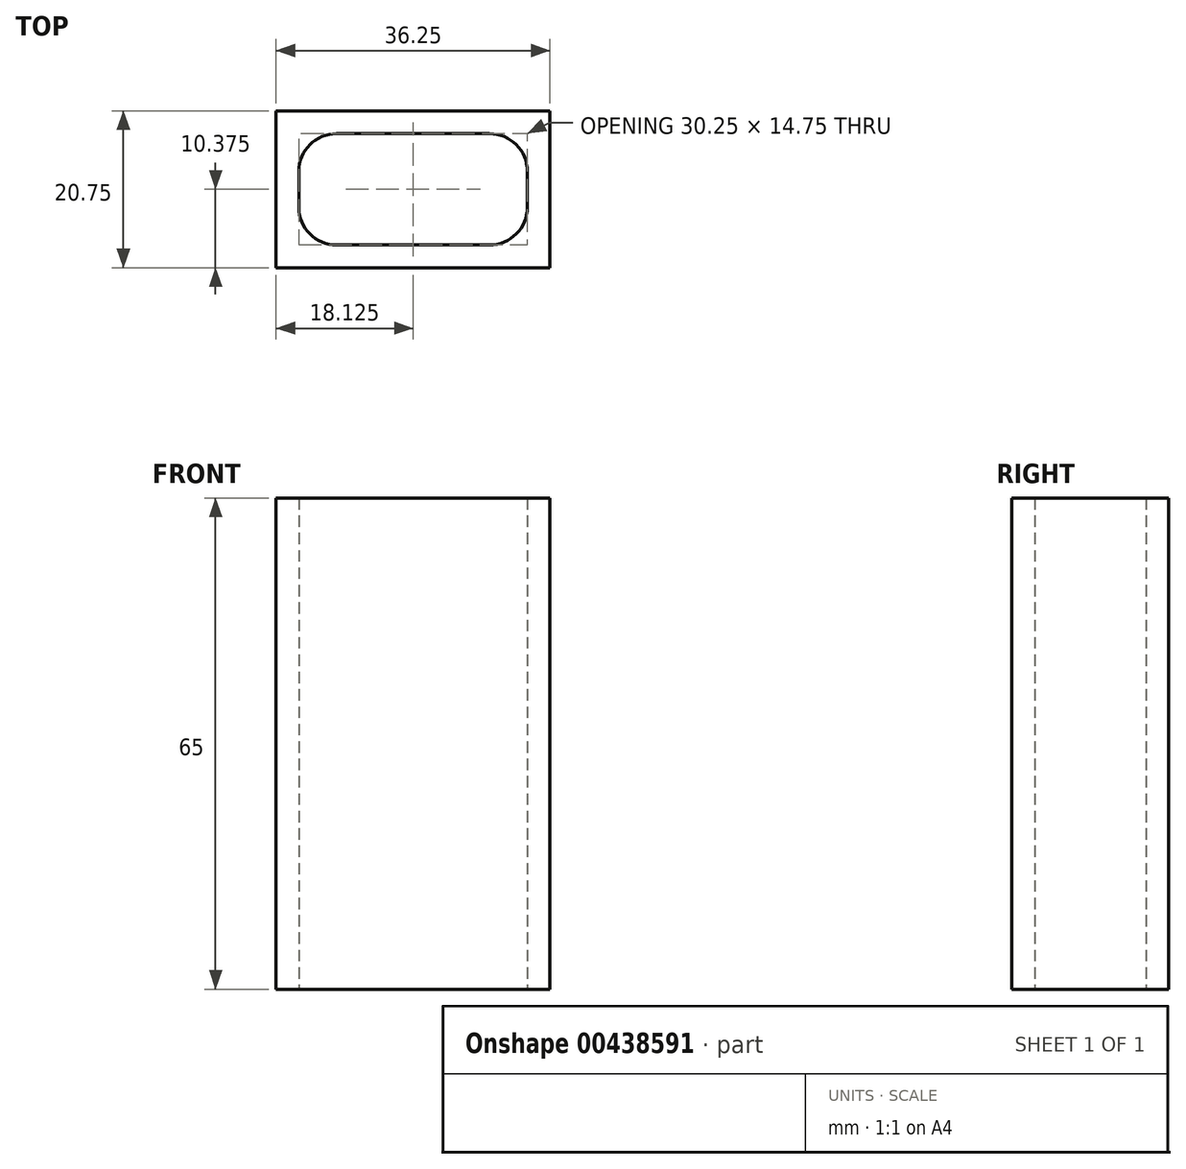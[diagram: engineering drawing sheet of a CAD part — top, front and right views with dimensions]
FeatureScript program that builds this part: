
annotation { "Feature Type Name" : "Feature", "Feature Type Description" : "" }
export const myFeature = defineFeature(function(context is Context, id is Id, definition is map)
    precondition{}
    {
        {
            var Q0;
            Q0=qCreatedBy(makeId("Top.planeOp"),FACE);
            var sketch = newSketch(context, id + "F0", { "sketchPlane" : qUnion([Q0])});
            skLineSegment(sketch, "E0.bottom", {"start": v(5, 0) * mm, "end": v(25.25, 0) * mm});
            skLineSegment(sketch, "E0.top", {"start": v(5, 14.75) * mm, "end": v(25.25, 14.75) * mm});
            skLineSegment(sketch, "E0.left", {"start": v(0, 5) * mm, "end": v(0, 9.75) * mm});
            skLineSegment(sketch, "E0.right", {"start": v(30.25, 5) * mm, "end": v(30.25, 9.75) * mm});
            skPoint(sketch, "E1.visualSharp", {"position": v(0, 14.75) * mm});
            skArc(sketch, "E1.filletArc", {"start": v(5, 14.75) * mm, "mid": v(1.46, 13.29) * mm, "end": v(0, 9.75) * mm});
            skPoint(sketch, "E2.visualSharp", {"position": v(30.25, 14.75) * mm});
            skArc(sketch, "E2.filletArc", {"start": v(30.25, 9.75) * mm, "mid": v(28.79, 13.29) * mm, "end": v(25.25, 14.75) * mm});
            skPoint(sketch, "E3.visualSharp", {"position": v(30.25, 0) * mm});
            skArc(sketch, "E3.filletArc", {"start": v(25.25, 0) * mm, "mid": v(28.79, 1.46) * mm, "end": v(30.25, 5) * mm});
            skPoint(sketch, "E4.visualSharp", {"position": v(0, 0) * mm});
            skArc(sketch, "E4.filletArc", {"start": v(0, 5) * mm, "mid": v(1.46, 1.46) * mm, "end": v(5, 0) * mm});
            skSolve(sketch);
        }
        {
            var Q0;
            Q0=makeQuery(id+"F0.imprint","IMPRINT",FACE,{"disambiguationData":[TD([[makeQuery(id+"F0.imprint","IMPRINT",EDGE,{"derivedFrom":sQuery(id+"F0.wireOp",EDGE,"E0.bottom")}),1.0]])]});
            var sketch = newSketch(context, id + "F1", { "sketchPlane" : qUnion([Q0])});
            skLineSegment(sketch, "E5.bottom", {"start": v(-3, -3) * mm, "end": v(33.25, -3) * mm});
            skLineSegment(sketch, "E5.top", {"start": v(-3, 17.75) * mm, "end": v(33.25, 17.75) * mm});
            skLineSegment(sketch, "E5.left", {"start": v(-3, -3) * mm, "end": v(-3, 17.75) * mm});
            skLineSegment(sketch, "E5.right", {"start": v(33.25, -3) * mm, "end": v(33.25, 17.75) * mm});
            skSolve(sketch);
        }
        {
            var Q0;
            Q0=makeQuery(id+"F1.imprint","IMPRINT",FACE,{"disambiguationData":[TD([[makeQuery(id+"F1.imprint","IMPRINT",EDGE,{"derivedFrom":sQuery(id+"F1.wireOp",EDGE,"E5.bottom")}),1.0]])]});
            extrude(context, id + "F2", {"entities" : qUnion([Q0]), "depth" : 65 * mm});
        }
    });
